# Revit family: Specialty_Equipment-Bavis_Fabacraft-Window_Drawer_Combo_Unit NEW
name_source: partatom
category: Specialty Equipment
units: mm (PartAtom-declared; Revit-internal decimal feet)

## family parameters
Always vertical = Yes
Cut with Voids When Loaded = No
Host = Wall
OmniClass Number = 23.40.70.27.24.21
OmniClass Title = Service and Teller Window Units
Part Type = Normal
Room Calculation Point = No
Round Connector Dimension = Use Diameter
Shared = No

## types (6) — shared parameters
10L = No
12L = No
Assembly Code = B2020100
C Center 1 = 0' - 0"
C Center 2 = 0' - 0"
C Counter Open Length = 0' - 11"
C Counter Open Width = 1' - 3 3/4"
Default Elevation = 0' - 0"
Depth = 0' - 6 3/4"
Drawer = Paint - Bavis Fabacraft - Red
Finish = Metal - Bavis Fabacraft - Aluminum - Dark Grey
Glazing = Glass - Bavis Fabacraft - Clear
Instruction Sheet Link = https://docs.bavis.com
Keynote = 08 51 00
Manufacturer = Bavis Fabacraft
Product Documentation Link = https://docs.bavis.com
Product Name = Bavis Window-Drawer Combination Unit
Product Page URL = https://www.bavis.com
URL = https://www.bavis.com
Version = 2020 - v1.0a
Video Link = https://www.youtube.com

## per-type parameters (varying)
| type | 60inch | C Drawer Location | C Drawer Start | Constraints | Counter Material | Height | Model | Rough Height | Rough Width | Teller Drawer Type | Warranty URL | Width |
| 32" Window with Counter - Electric Drawer | No | 0' - 0" | 0' - 0 115/128" | 32 | Metal - Bavis Fabacraft -Aluminum | 4' - 1" | 12000992-5000 Tank | 4' - 1 1/4" | 2' - 9 1/2" | Specialty_Equipment-Bavis_Fabacraft-Electric_Transaction_Drawer : Large |  | 2' - 9" |
| 50" Window with Counter - Electric Drawer | No | 0' - 8 1/4" | 0' - 0 115/128" | 50 | Metal - Bavis Fabacraft -Aluminum | 4' - 11 3/8" | 12001017-5000 Tank | 4' - 11 5/8" | 4' - 2 1/4" | Specialty_Equipment-Bavis_Fabacraft-Electric_Transaction_Drawer : Large |  | 4' - 1 3/4" |
| 60" Window with Counter - Electric Drawer | Yes | 0' - 0" | 0' - 3 1/2" | 60 | Counter - Bavis Fabacraft - Almond | 4' - 0" | 12000993-5000 Tank | 4' - 0 1/4" | 4' - 8 1/2" | Specialty_Equipment-Bavis_Fabacraft-Electric_Transaction_Drawer : Large | Contact Manufacturer for Warranty Information | 4' - 8" |
| 32" Window with Counter - Manual Drawer | No | 0' - 0" | 0' - 0 115/128" | 32 | Metal - Bavis Fabacraft -Aluminum | 4' - 1" | 12000992-MD | 4' - 1 1/4" | 2' - 9 1/2" | Specialty_Equipment-Bavis_Fabacraft-Manual_Transaction_Drawer : Manual Transaction Drawer |  | 2' - 9" |
| 50" Window with Counter - Manual Drawer | No | 0' - 8 1/4" | 0' - 0 115/128" | 50 | Metal - Bavis Fabacraft -Aluminum | 4' - 11 3/8" | 12001017-MD | 4' - 11 5/8" | 4' - 2 1/4" | Specialty_Equipment-Bavis_Fabacraft-Manual_Transaction_Drawer : Manual Transaction Drawer |  | 4' - 1 3/4" |
| 60" Window with Counter - Manual Drawer | Yes | 0' - 0" | 0' - 0 115/128" | 60 | Counter - Bavis Fabacraft - Almond | 4' - 0" | 12000993-MD | 4' - 0 1/4" | 4' - 8 1/2" | Specialty_Equipment-Bavis_Fabacraft-Manual_Transaction_Drawer : Manual Transaction Drawer |  | 4' - 8" |

## geometry (parser evidence)
native form markers: Sweep x21
no freeform markers — native parametric forms only
